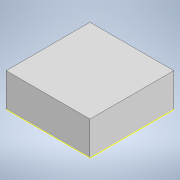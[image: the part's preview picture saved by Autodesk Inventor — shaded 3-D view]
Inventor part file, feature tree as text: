
AUTODESK INVENTOR PART (.ipt)
format: ipt  version: 2022 (Build 260153000, 153)  size: 150,016 bytes
history: native  units: in
note: dims shown in document units (in); Inventor stores cm internally (conversion verified against a paired STEP export)
features: extrude x6, sketch x6, projected_geometry x2, shell x1
ambient origin geometry x8: Origin, YZ Plane, XZ Plane, XY Plane, X Axis, Y Axis, Z Axis, Center Point
bodies: Solid1 (feature_tree)
feature tree (15):
  extrude  "Extrusion1"  Depth=0.1969in
  shell  "Shell1"  Thickness=0.3937in
  extrude  "Extrusion2"  Depth=0.0197in
  sketch  "Sketch3"  dims[d6=0.0394in d7=0.0in d8=0.0in d9=0.0in]
  extrude  "Extrusion3"  TaperAngle=0.0deg  [1 undecoded]
  extrude  "Extrusion4"  Depth=0.0591in
  sketch  "Sketch4"  dims[d10=0.0591in d11=0.0in d12=0.0079in]
  extrude  "Extrusion5"  Depth=0.0197in TaperAngle=0.0deg
  extrude  "Extrusion6"  [1 undecoded]
  sketch  "Sketch1"  dims[d0=0.1969in d1=0.1969in d2=0.3937in d3=0.0in]
  sketch  "Sketch2"  dims[d4=0.0394in d5=0.0197in]
  projected_geometry  "Projected Loop1"
  projected_geometry  "Projected Loop2"
  sketch  "Sketch5"  dims[d13=0.0591in d14=0.0in d15=0.0197in d16=0.0in]
  sketch  "Sketch6"
note: 2 required parameter values undecoded (feature->parameter linkage not recoverable at this tier; creation-order binding heuristic only, values carry confidence <= 0.55)
